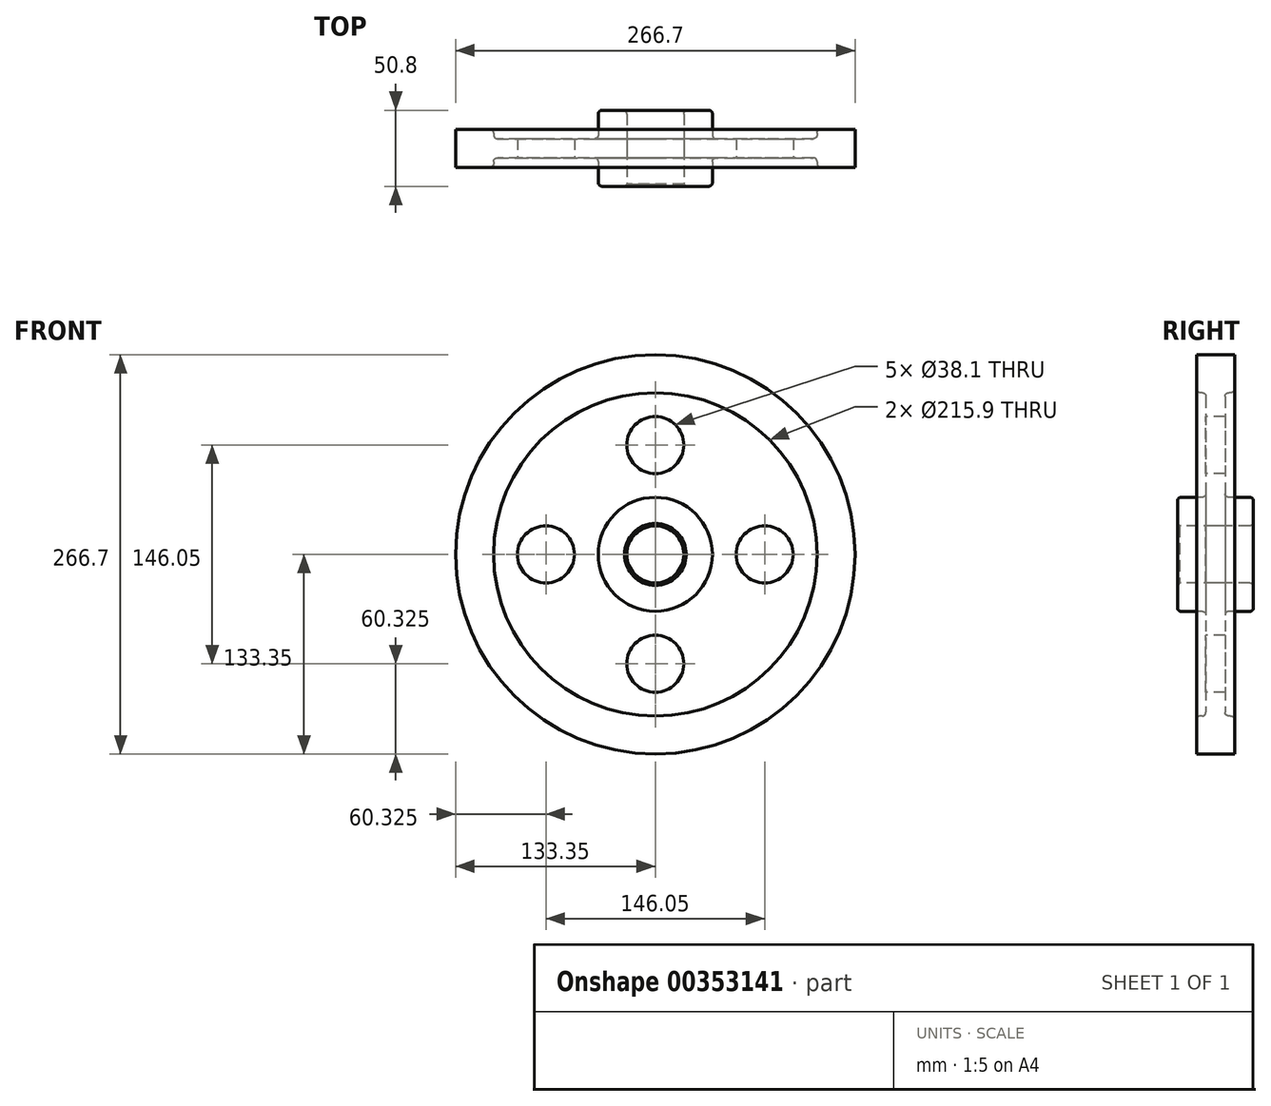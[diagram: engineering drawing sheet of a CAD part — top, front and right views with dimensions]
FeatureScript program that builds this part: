
annotation { "Feature Type Name" : "Feature", "Feature Type Description" : "" }
export const myFeature = defineFeature(function(context is Context, id is Id, definition is map)
    precondition{}
    {
        {
            var Q0;
            Q0=qCreatedBy(makeId("Right.planeOp"),FACE);
            var sketch = newSketch(context, id + "F0", { "sketchPlane" : qUnion([Q0])});
            skLineSegment(sketch, "E0", {"start": v(0, 0) * mm, "end": v(144.44, 0) * mm, "construction": true});
            skLineSegment(sketch, "E1.0", {"start": v(0, 19.05) * mm, "end": v(25.4, 19.05) * mm});
            skLineSegment(sketch, "E2.0", {"start": v(6.35, 38.1) * mm, "end": v(25.4, 38.1) * mm});
            skLineSegment(sketch, "E3.0", {"start": v(6.35, 107.95) * mm, "end": v(12.7, 107.95) * mm, "construction": true});
            skLineSegment(sketch, "E4.0", {"start": v(0, 133.35) * mm, "end": v(12.7, 133.35) * mm});
            skLineSegment(sketch, "E5", {"start": v(0, 133.35) * mm, "end": v(0, 0) * mm, "construction": true});
            skLineSegment(sketch, "E6.0", {"start": v(6.35, 107.95) * mm, "end": v(6.35, 38.1) * mm});
            skLineSegment(sketch, "E7.0", {"start": v(12.7, 133.35) * mm, "end": v(12.7, 107.95) * mm});
            skLineSegment(sketch, "E8", {"start": v(25.4, 38.1) * mm, "end": v(25.4, 19.05) * mm});
            skLineSegment(sketch, "E9.MirrorCS", {"start": v(12.7, 133.35) * mm, "end": v(0, 133.35) * mm});
            skLineSegment(sketch, "E10.MirrorCS", {"start": v(12.7, 19.05) * mm, "end": v(0, 19.05) * mm});
            skLineSegment(sketch, "E11", {"start": v(6.35, 107.95) * mm, "end": v(12.7, 107.95) * mm});
            skLineSegment(sketch, "E12.MirrorCS", {"start": v(0, 133.35) * mm, "end": v(0, 107.95) * mm});
            skPoint(sketch, "E13.MirrorCS.end.orphan", {"position": v(0, 107.95) * mm});
            skPoint(sketch, "E13.MirrorCS.start.orphan", {"position": v(6.35, 107.95) * mm});
            skPoint(sketch, "E14.orphan", {"position": v(6.35, 38.1) * mm});
            skPoint(sketch, "E15.MirrorCS.end.orphan", {"position": v(-12.7, 38.1) * mm});
            skPoint(sketch, "E16.orphan", {"position": v(-12.7, 19.05) * mm});
            skPoint(sketch, "E17.MirrorCS.start.orphan", {"position": v(12.7, 19.05) * mm});
            skLineSegment(sketch, "E18", {"start": v(25.4, 38.1) * mm, "end": v(6.35, 38.1) * mm});
            skLineSegment(sketch, "E19.MirrorCS", {"start": v(-12.7, 133.35) * mm, "end": v(0, 133.35) * mm});
            skLineSegment(sketch, "E20.MirrorCS", {"start": v(-12.7, 133.35) * mm, "end": v(-12.7, 107.95) * mm});
            skLineSegment(sketch, "E21.MirrorCS", {"start": v(-6.35, 107.95) * mm, "end": v(-12.7, 107.95) * mm});
            skLineSegment(sketch, "E22.MirrorCS", {"start": v(-6.35, 107.95) * mm, "end": v(-6.35, 38.1) * mm});
            skLineSegment(sketch, "E23.MirrorCS", {"start": v(-6.35, 38.1) * mm, "end": v(-25.4, 38.1) * mm});
            skLineSegment(sketch, "E24.MirrorCS", {"start": v(-25.4, 38.1) * mm, "end": v(-25.4, 19.05) * mm});
            skLineSegment(sketch, "E25.MirrorCS", {"start": v(0, 19.05) * mm, "end": v(-25.4, 19.05) * mm});
            skSolve(sketch);
        }
        {
            var Q0;
            Q0=makeQuery(id+"F0.imprint","IMPRINT",FACE,{"disambiguationData":[TD([[makeQuery(id+"F0.imprint","IMPRINT",EDGE,{"derivedFrom":sQuery(id+"F0.wireOp",EDGE,"E6.0")}),-1.0]])]});
            var Q1;
            Q1=sQuery(id+"F0.wireOp",EDGE,"E0");
            revolve(context, id + "F1", {"entities" : qUnion([Q0]), "axis" : qUnion([Q1]), "revolveType" : RevolveType.FULL});
        }
        {
            var Q0;
            Q0=makeQuery(id+"F1.opRevolve","SWEPT_FACE",FACE,{"disambiguationData":[OSD([sQuery(id+"F0.wireOp",EDGE,"E22.MirrorCS")])]});
            var sketch = newSketch(context, id + "F2", { "sketchPlane" : qUnion([Q0])});
            skLineSegment(sketch, "E26", {"start": v(0, 0) * mm, "end": v(0, 73.03) * mm});
            skCircle(sketch, "E27", {"center": v(0, 73.03) * mm, "radius": 19.05 * mm});
            skCircle(sketch, "E28.1.0", {"center": v(-73.03, 0) * mm, "radius": 19.05 * mm});
            skCircle(sketch, "E28.2.0", {"center": v(0, -73.03) * mm, "radius": 19.05 * mm});
            skCircle(sketch, "E28.3.0", {"center": v(73.03, 0) * mm, "radius": 19.05 * mm});
            skPoint(sketch, "E28.center", {"position": v(0, 0) * mm});
            skSolve(sketch);
        }
        {
            var Q0;
            Q0=makeQuery(id+"F2.imprint","IMPRINT",FACE,{"disambiguationData":[TD([[makeQuery(id+"F2.imprint","IMPRINT",EDGE,{"derivedFrom":sQuery(id+"F2.wireOp",EDGE,"E28.3.0")}),1.0]])]});
            var Q1;
            Q1=makeQuery(id+"F2.imprint","IMPRINT",FACE,{"disambiguationData":[TD([[makeQuery(id+"F2.imprint","IMPRINT",EDGE,{"derivedFrom":sQuery(id+"F2.wireOp",EDGE,"E27")}),1.0]])]});
            var Q2;
            Q2=makeQuery(id+"F2.imprint","IMPRINT",FACE,{"disambiguationData":[TD([[makeQuery(id+"F2.imprint","IMPRINT",EDGE,{"derivedFrom":sQuery(id+"F2.wireOp",EDGE,"E28.1.0")}),1.0]])]});
            var Q3;
            Q3=makeQuery(id+"F2.imprint","IMPRINT",FACE,{"disambiguationData":[TD([[makeQuery(id+"F2.imprint","IMPRINT",EDGE,{"derivedFrom":sQuery(id+"F2.wireOp",EDGE,"E28.2.0")}),1.0]])]});
            extrude(context, id + "F3", {"entities" : qUnion([Q0, Q1, Q2, Q3]), "operationType" : NewBodyOperationType.REMOVE, "depth" : 25.4 * mm});
        }
        {
            var Q0;
            Q0 = qSketchRegion(id + "F2", true);
            extrude(context, id + "F4", {"entities" : qUnion([Q0]), "operationType" : NewBodyOperationType.REMOVE, "oppositeDirection" : true, "depth" : 25.4 * mm});
        }
        {
            var Q0;
            Q0=makeQuery(id+"F1.opRevolve","SWEPT_EDGE",EDGE,{"disambiguationData":[OSD([sQuery(id+"F0.wireOp",EDGE,"E20.MirrorCS"),sQuery(id+"F0.wireOp",EDGE,"E21.MirrorCS")])]});
            var Q1;
            Q1=makeQuery(id+"F1.opRevolve","SWEPT_EDGE",EDGE,{"disambiguationData":[OSD([sQuery(id+"F0.wireOp",EDGE,"E21.MirrorCS"),sQuery(id+"F0.wireOp",EDGE,"E22.MirrorCS")])]});
            var Q2;
            Q2=makeQuery(id+"F1.opRevolve","SWEPT_EDGE",EDGE,{"disambiguationData":[OSD([sQuery(id+"F0.wireOp",EDGE,"E22.MirrorCS"),sQuery(id+"F0.wireOp",EDGE,"E23.MirrorCS")])]});
            var Q3;
            Q3=makeQuery(id+"F1.opRevolve","SWEPT_EDGE",EDGE,{"disambiguationData":[OSD([sQuery(id+"F0.wireOp",EDGE,"E23.MirrorCS"),sQuery(id+"F0.wireOp",EDGE,"E24.MirrorCS")])]});
            fillet(context, id + "F5", {"entities" : qUnion([Q0, Q1, Q2, Q3]), "radius" : 2.54 * mm, "tangentPropagation" : true, "allowEdgeOverflow" : false});
        }
        {
            var Q0;
            Q0=makeQuery(id+"F1.opRevolve","SWEPT_EDGE",EDGE,{"disambiguationData":[OSD([sQuery(id+"F0.wireOp",EDGE,"E6.0"),sQuery(id+"F0.wireOp",EDGE,"E11")])]});
            var Q1;
            Q1=makeQuery(id+"F1.opRevolve","SWEPT_EDGE",EDGE,{"disambiguationData":[OSD([sQuery(id+"F0.wireOp",EDGE,"E7.0"),sQuery(id+"F0.wireOp",EDGE,"E11")])]});
            var Q2;
            Q2=makeQuery(id+"F1.opRevolve","SWEPT_EDGE",EDGE,{"disambiguationData":[OSD([sQuery(id+"F0.wireOp",EDGE,"E8"),sQuery(id+"F0.wireOp",EDGE,"E18")])]});
            var Q3;
            Q3=makeQuery(id+"F1.opRevolve","SWEPT_EDGE",EDGE,{"disambiguationData":[OSD([sQuery(id+"F0.wireOp",EDGE,"E6.0"),sQuery(id+"F0.wireOp",EDGE,"E18")])]});
            fillet(context, id + "F6", {"entities" : qUnion([Q0, Q1, Q2, Q3]), "radius" : 2.54 * mm, "tangentPropagation" : true, "allowEdgeOverflow" : false});
        }
        {
            var Q0;
            Q0=makeQuery(id+"F1.opRevolve","SWEPT_EDGE",EDGE,{"disambiguationData":[OSD([sQuery(id+"F0.wireOp",EDGE,"E24.MirrorCS"),sQuery(id+"F0.wireOp",EDGE,"E25.MirrorCS")])]});
            var Q1;
            Q1=makeQuery(id+"F1.opRevolve","SWEPT_FACE",FACE,{"disambiguationData":[OSD([sQuery(id+"F0.wireOp",EDGE,"E1.0"),sQuery(id+"F0.wireOp",EDGE,"E25.MirrorCS")])]});
            chamfer(context, id + "F7", {"entities" : qUnion([Q0, Q1]), "width" : 1.59 * mm, "tangentPropagation" : true});
        }
    });
